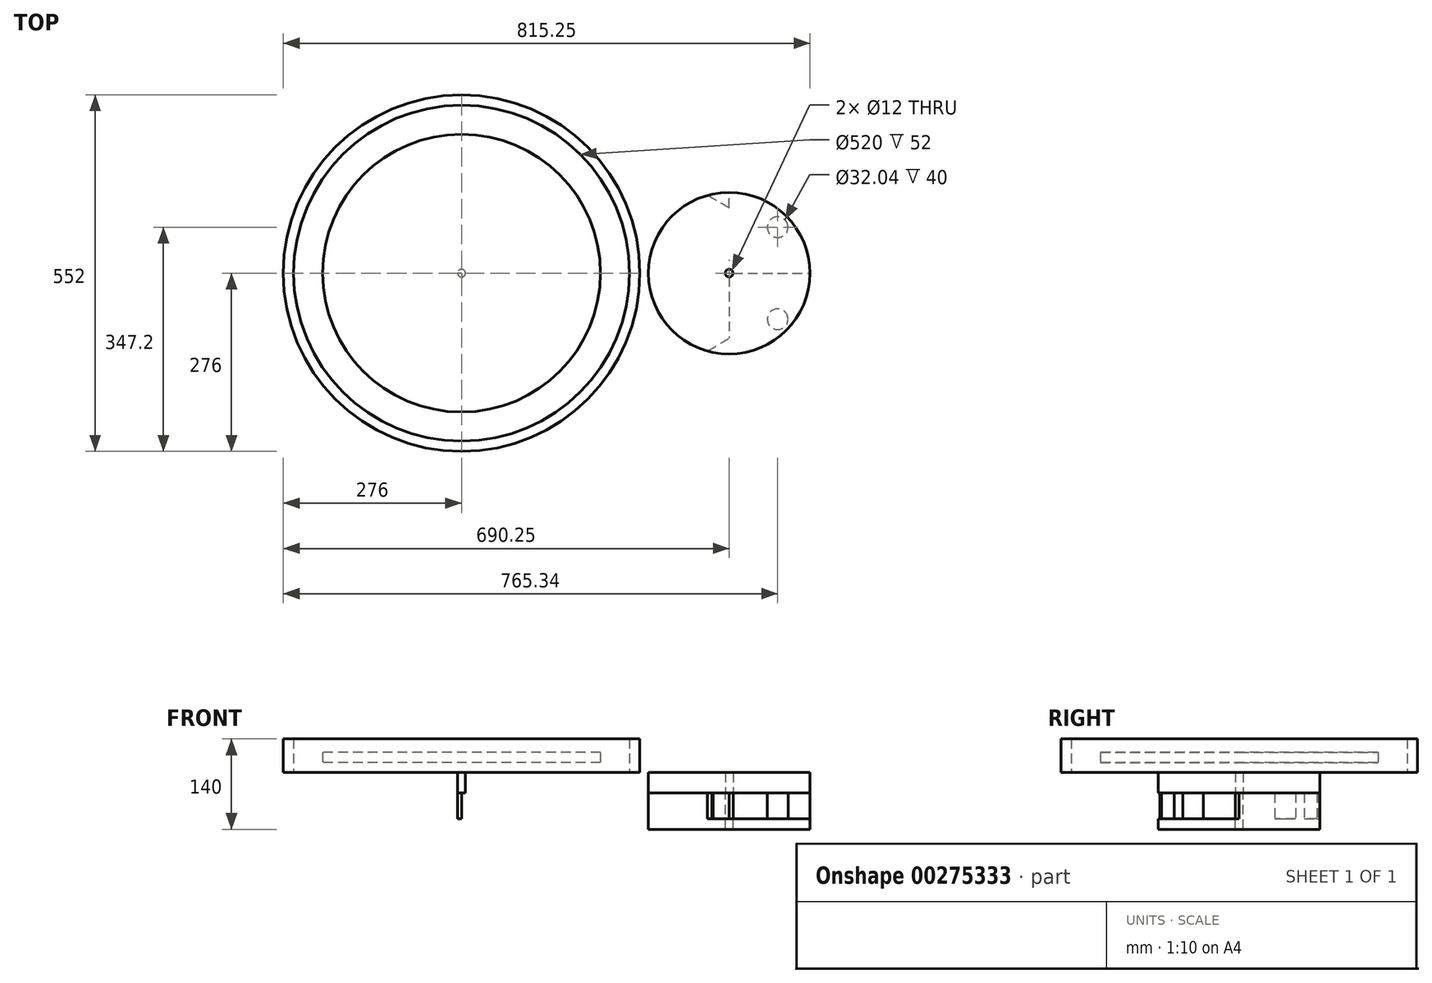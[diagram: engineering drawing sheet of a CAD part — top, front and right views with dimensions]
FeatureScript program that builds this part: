
annotation { "Feature Type Name" : "Feature", "Feature Type Description" : "" }
export const myFeature = defineFeature(function(context is Context, id is Id, definition is map)
    precondition{}
    {
        {
            var Q0;
            Q0=qCreatedBy(makeId("Top.planeOp"),FACE);
            var sketch = newSketch(context, id + "F0", { "sketchPlane" : qUnion([Q0])});
            skCircle(sketch, "E0", {"center": v(0, 0) * mm, "radius": 215 * mm});
            skCircle(sketch, "E1", {"center": v(0, 0) * mm, "radius": 260 * mm});
            skCircle(sketch, "E2", {"center": v(0, 0) * mm, "radius": 276 * mm});
            skSolve(sketch);
        }
        {
            var Q0;
            Q0=makeQuery(id+"F0.imprint","IMPRINT",FACE,{"disambiguationData":[TD([[makeQuery(id+"F0.imprint","IMPRINT",EDGE,{"derivedFrom":sQuery(id+"F0.wireOp",EDGE,"E0")}),1.0]])]});
            extrude(context, id + "F1", {"entities" : qUnion([Q0]), "depth" : 15 * mm});
        }
        {
            var Q0;
            Q0=makeQuery(id+"F1.opExtrude","CAP_FACE",FACE,{"disambiguationData":[OSD([sQuery(id+"F0.wireOp",EDGE,"E0")])],"isStart":false});
            extrude(context, id + "F2", {"entities" : qUnion([Q0]), "depth" : 16 * mm});
        }
        {
            var Q0;
            Q0=makeQuery(id+"F1.opExtrude","CAP_FACE",FACE,{"disambiguationData":[OSD([sQuery(id+"F0.wireOp",EDGE,"E0")])],"isStart":true});
            extrude(context, id + "F3", {"entities" : qUnion([Q0]), "operationType" : NewBodyOperationType.REMOVE, "oppositeDirection" : true, "depth" : 15 * mm});
        }
        {
            var Q0;
            Q0=makeQuery(id+"F0.imprint","IMPRINT",FACE,{"disambiguationData":[TD([[makeQuery(id+"F0.imprint","IMPRINT",EDGE,{"derivedFrom":sQuery(id+"F0.wireOp",EDGE,"E1")}),-1.0]])]});
            extrude(context, id + "F4", {"entities" : qUnion([Q0]), "depth" : 52 * mm});
        }
        {
            var Q0;
            Q0=qCreatedBy(makeId("Front.planeOp"),FACE);
            var sketch = newSketch(context, id + "F5", { "sketchPlane" : qUnion([Q0])});
            skLineSegment(sketch, "E3.bottom", {"start": v(0, 0) * mm, "end": v(-275.72, 0) * mm});
            skLineSegment(sketch, "E3.left", {"start": v(0, 0) * mm, "end": v(0, -16) * mm});
            skLineSegment(sketch, "E3.right", {"start": v(-275.72, 0) * mm, "end": v(-275.72, -16) * mm});
            skLineSegment(sketch, "E4.top", {"start": v(-275.72, -32) * mm, "end": v(0, -32) * mm});
            skLineSegment(sketch, "E4.left", {"start": v(-275.72, -16) * mm, "end": v(-275.72, -32) * mm});
            skLineSegment(sketch, "E4.right", {"start": v(0, -16) * mm, "end": v(0, -32) * mm});
            skFitSpline(sketch, "E5", {"points": [v(-259.93, 0) * mm, v(-213.05, -20.4) * mm, v(-60.25, 0) * mm], "startDerivative": vector(75.22, -131.35) * mm, "endDerivative": vector(230.25, 0) * mm});
            skLineSegment(sketch, "E6", {"start": v(-275.72, 0) * mm, "end": v(-259.93, 0) * mm});
            skLineSegment(sketch, "E7", {"start": v(0, 0) * mm, "end": v(-60.25, 0) * mm});
            skLineSegment(sketch, "E8", {"start": v(-275.72, 0) * mm, "end": v(-275.72, -32) * mm});
            skLineSegment(sketch, "E9.bottom", {"start": v(0, -32) * mm, "end": v(-6, -32) * mm});
            skLineSegment(sketch, "E9.top", {"start": v(0, 0) * mm, "end": v(-6, 0) * mm});
            skLineSegment(sketch, "E9.left", {"start": v(0, -32) * mm, "end": v(0, 0) * mm});
            skLineSegment(sketch, "E9.right", {"start": v(-6, -32) * mm, "end": v(-6, 0) * mm});
            skSolve(sketch);
        }
        {
            var Q0;
            Q0=makeQuery(id+"F5.imprint","IMPRINT",FACE,{"disambiguationData":[TD([[makeQuery(id+"F5.imprint","IMPRINT",EDGE,{"derivedFrom":sQuery(id+"F5.wireOp",EDGE,"E4.top")}),1.0]])]});
            var Q1;
            Q1=sQuery(id+"F5.wireOp",EDGE,"E4.right");
            revolve(context, id + "F6", {"entities" : qUnion([Q0]), "axis" : qUnion([Q1]), "revolveType" : RevolveType.FULL});
        }
        {
            var Q0;
            Q0=makeQuery(id+"F6.opRevolve","SWEPT_FACE",FACE,{"disambiguationData":[OSD([sQuery(id+"F5.wireOp",EDGE,"E4.top")])]});
            var sketch = newSketch(context, id + "F7", { "sketchPlane" : qUnion([Q0])});
            skCircle(sketch, "E10", {"center": v(414.25, 0) * mm, "radius": 125 * mm});
            skFitSpline(sketch, "E11", {"points": [v(501.83, 89.19) * mm, v(274.86, 218) * mm, v(0, 275.72) * mm], "startDerivative": vector(-181.97, 266.91) * mm, "endDerivative": vector(-537.63, 15.29) * mm});
            skLineSegment(sketch, "E12", {"start": v(414.25, 0) * mm, "end": v(0, 0) * mm});
            skFitSpline(sketch, "E13.MirrorCS", {"points": [v(501.83, -89.19) * mm, v(274.86, -218) * mm, v(0, -275.72) * mm], "startDerivative": vector(-181.97, -266.91) * mm, "endDerivative": vector(-537.63, -15.29) * mm});
            skFitSpline(sketch, "E14.MirrorCS", {"points": [v(501.83, -89.19) * mm, v(274.86, -218) * mm, v(0, -275.72) * mm], "startDerivative": vector(-181.97, -266.91) * mm, "endDerivative": vector(-537.63, -15.29) * mm});
            skLineSegment(sketch, "E15", {"start": v(0, 261.43) * mm, "end": v(0, 275.72) * mm});
            skLineSegment(sketch, "E16", {"start": v(0, -262.66) * mm, "end": v(0, -275.72) * mm});
            skArc(sketch, "E17", {"start": v(0, -262.66) * mm, "mid": v(263.36, -0.62) * mm, "end": v(0, 261.43) * mm});
            skCircle(sketch, "E18", {"center": v(414.25, 0) * mm, "radius": 6 * mm});
            skSolve(sketch);
        }
        {
            var Q0;
            Q0 = qSketchRegion(id + "F7", true);
            extrude(context, id + "F8", {"entities" : qUnion([Q0]), "operationType" : NewBodyOperationType.ADD, "oppositeDirection" : true, "depth" : 32 * mm});
        }
        {
            var Q0;
            Q0=makeQuery(id+"F8.boolean.opBoolean","MERGE",FACE,{"derivedFrom":[makeQuery(id+"F6.opRevolve","SWEPT_FACE",FACE,{"disambiguationData":[OSD([sQuery(id+"F5.wireOp",EDGE,"E4.top")])]}),makeQuery(id+"F8.opExtrude","CAP_FACE",FACE,{"disambiguationData":[OSD([sQuery(id+"F7.wireOp",EDGE,"E10"),sQuery(id+"F7.wireOp",EDGE,"E11"),sQuery(id+"F7.wireOp",EDGE,"E14.MirrorCS"),sQuery(id+"F7.wireOp",EDGE,"E15"),sQuery(id+"F7.wireOp",EDGE,"E16"),sQuery(id+"F7.wireOp",EDGE,"E17"),sQuery(id+"F7.wireOp",EDGE,"E18")])],"isStart":true})]});
            extrude(context, id + "F9", {"entities" : qUnion([Q0]), "depth" : 40 * mm});
        }
        {
            var Q0;
            Q0=makeQuery(id+"F9.opExtrude","CAP_FACE",FACE,{"disambiguationData":[OSD([sQuery(id+"F5.wireOp",EDGE,"E4.top"),sQuery(id+"F7.wireOp",EDGE,"E10"),sQuery(id+"F7.wireOp",EDGE,"E11"),sQuery(id+"F7.wireOp",EDGE,"E14.MirrorCS"),sQuery(id+"F7.wireOp",EDGE,"E15"),sQuery(id+"F7.wireOp",EDGE,"E16"),sQuery(id+"F7.wireOp",EDGE,"E17"),sQuery(id+"F7.wireOp",EDGE,"E18")])],"isStart":false});
            extrude(context, id + "F10", {"entities" : qUnion([Q0]), "depth" : 16 * mm});
        }
        {
            var Q0;
            Q0=makeQuery(id+"F9.opExtrude","CAP_FACE",FACE,{"disambiguationData":[OSD([sQuery(id+"F5.wireOp",EDGE,"E4.top"),sQuery(id+"F7.wireOp",EDGE,"E10"),sQuery(id+"F7.wireOp",EDGE,"E11"),sQuery(id+"F7.wireOp",EDGE,"E14.MirrorCS"),sQuery(id+"F7.wireOp",EDGE,"E15"),sQuery(id+"F7.wireOp",EDGE,"E16"),sQuery(id+"F7.wireOp",EDGE,"E17"),sQuery(id+"F7.wireOp",EDGE,"E18")])],"isStart":false});
            var sketch = newSketch(context, id + "F11", { "sketchPlane" : qUnion([Q0])});
            skCircle(sketch, "E19", {"center": v(0, 0) * mm, "radius": 249 * mm});
            skLineSegment(sketch, "E20", {"start": v(0, 0) * mm, "end": v(-303.54, 0) * mm});
            skPoint(sketch, "E20.endSnap0", {"position": v(-275.72, 0) * mm});
            skLineSegment(sketch, "E21", {"start": v(0, 0) * mm, "end": v(543.1, 0) * mm});
            skPoint(sketch, "E21.endSnap0", {"position": v(539.25, 0) * mm});
            skLineSegment(sketch, "E22", {"start": v(0, 0) * mm, "end": v(0, 284.87) * mm});
            skLineSegment(sketch, "E23", {"start": v(414.25, 0) * mm, "end": v(414.25, 300.96) * mm});
            skLineSegment(sketch, "E24.MirrorCS", {"start": v(414.25, 0) * mm, "end": v(414.25, -300.96) * mm});
            skLineSegment(sketch, "E25.MirrorCS", {"start": v(0, 0) * mm, "end": v(0, -284.87) * mm});
            skArc(sketch, "E26", {"start": v(-260.03, 91.7) * mm, "mid": v(-252.24, 72.81) * mm, "end": v(-234.67, 83.25) * mm});
            skArc(sketch, "E27", {"start": v(-30.78, 247.1) * mm, "mid": v(-22.5, 263.6) * mm, "end": v(-38.37, 273.04) * mm});
            skArc(sketch, "E28.MirrorCS", {"start": v(-30.78, -247.1) * mm, "mid": v(-22.5, -263.6) * mm, "end": v(-38.37, -273.04) * mm});
            skArc(sketch, "E29.MirrorCS", {"start": v(-260.03, -91.7) * mm, "mid": v(-252.24, -72.81) * mm, "end": v(-234.67, -83.25) * mm});
            skArc(sketch, "E30", {"start": v(462.1, 69.9) * mm, "mid": v(241.34, 186) * mm, "end": v(0, 249) * mm});
            skArc(sketch, "E31", {"start": v(373.84, 124.15) * mm, "mid": v(405.14, 135.2) * mm, "end": v(394.09, 166.5) * mm});
            skArc(sketch, "E32", {"start": v(191.52, 245.4) * mm, "mid": v(166.7, 232.73) * mm, "end": v(179.37, 207.9) * mm});
            skArc(sketch, "E33.MirrorCS", {"start": v(191.52, -245.4) * mm, "mid": v(166.7, -232.73) * mm, "end": v(179.37, -207.9) * mm});
            skArc(sketch, "E34.MirrorCS", {"start": v(462.1, -69.9) * mm, "mid": v(241.34, -186) * mm, "end": v(0, -249) * mm});
            skArc(sketch, "E35.MirrorCS", {"start": v(373.84, -124.15) * mm, "mid": v(405.14, -135.2) * mm, "end": v(394.09, -166.5) * mm});
            skCircle(sketch, "E36", {"center": v(489.34, 71.2) * mm, "radius": 16.02 * mm});
            skCircle(sketch, "E37.MirrorC", {"center": v(489.34, -71.2) * mm, "radius": 16.02 * mm});
            skSolve(sketch);
        }
        {
            var Q0;
            {var subQ1=sQuery(id+"F11.wireOp",EDGE,"E33.MirrorCS");Q0=makeQuery(id+"F11.imprint","IMPRINT",FACE,{"disambiguationData":[TD([[makeQuery(id+"F11.imprint","IMPRINT",EDGE,{"derivedFrom":subQ1}),1.0]])]});}
            var Q1;
            {var subQ6=sQuery(id+"F11.wireOp",EDGE,"E19");var subQ8=sQuery(id+"F11.wireOp",EDGE,"E21");var subQ10=makeQuery(id+"F11.imprint","INTERSECT",VERTEX,{"derivedFrom":[subQ6,subQ8]});Q1=makeQuery(id+"F11.imprint","IMPRINT",FACE,{"disambiguationData":[TD([[makeQuery(id+"F11.imprint","IMPRINT",EDGE,{"disambiguationData":[TD([[subQ10,1.0]])],"derivedFrom":subQ6}),-1.0]])]});}
            var Q2;
            {var subQ2=sQuery(id+"F11.wireOp",EDGE,"E19");var subQ7=sQuery(id+"F11.wireOp",EDGE,"E21");var subQ8=makeQuery(id+"F11.imprint","INTERSECT",VERTEX,{"derivedFrom":[subQ2,subQ7]});Q2=makeQuery(id+"F11.imprint","IMPRINT",FACE,{"disambiguationData":[TD([[makeQuery(id+"F11.imprint","IMPRINT",EDGE,{"disambiguationData":[TD([[subQ8,1.0]])],"derivedFrom":subQ2}),1.0]])]});}
            var Q3;
            Q3=makeQuery(id+"F11.imprint","IMPRINT",FACE,{"disambiguationData":[TD([[makeQuery(id+"F11.imprint","IMPRINT",EDGE,{"derivedFrom":sQuery(id+"F11.wireOp",EDGE,"E37.MirrorC")}),1.0]])]});
            var Q4;
            {var subQ0=sQuery(id+"F11.wireOp",EDGE,"E34.MirrorCS");var subQ1=sQuery(id+"F11.wireOp",EDGE,"E24.MirrorCS");var subQ2=makeQuery(id+"F11.imprint","INTERSECT",VERTEX,{"derivedFrom":[subQ1,subQ0]});Q4=makeQuery(id+"F11.imprint","IMPRINT",FACE,{"disambiguationData":[TD([[makeQuery(id+"F11.imprint","IMPRINT",EDGE,{"disambiguationData":[TD([[subQ2,-1.0]])],"derivedFrom":subQ1}),-1.0]])]});}
            var Q5;
            {var subQ0=sQuery(id+"F11.wireOp",EDGE,"E20");var subQ1=sQuery(id+"F11.wireOp",EDGE,"E19");var subQ2=makeQuery(id+"F11.imprint","INTERSECT",VERTEX,{"derivedFrom":[subQ1,subQ0]});Q5=makeQuery(id+"F11.imprint","IMPRINT",FACE,{"disambiguationData":[TD([[makeQuery(id+"F11.imprint","IMPRINT",EDGE,{"disambiguationData":[TD([[subQ2,-1.0]])],"derivedFrom":subQ1}),1.0]])]});}
            var Q6;
            {var subQ0=sQuery(id+"F11.wireOp",EDGE,"E28.MirrorCS");var subQ1=sQuery(id+"F11.wireOp",EDGE,"E19");var subQ2=makeQuery(id+"F11.imprint","INTERSECT",VERTEX,{"derivedFrom":[subQ1,subQ0]});Q6=makeQuery(id+"F11.imprint","IMPRINT",FACE,{"disambiguationData":[TD([[makeQuery(id+"F11.imprint","IMPRINT",EDGE,{"disambiguationData":[TD([[subQ2,-1.0]])],"derivedFrom":subQ1}),-1.0]])]});}
            var Q7;
            {var subQ0=sQuery(id+"F11.wireOp",EDGE,"E20");var subQ1=sQuery(id+"F11.wireOp",EDGE,"E19");var subQ2=makeQuery(id+"F11.imprint","INTERSECT",VERTEX,{"derivedFrom":[subQ1,subQ0]});Q7=makeQuery(id+"F11.imprint","IMPRINT",FACE,{"disambiguationData":[TD([[makeQuery(id+"F11.imprint","IMPRINT",EDGE,{"disambiguationData":[TD([[subQ2,-1.0]])],"derivedFrom":subQ1}),-1.0]])]});}
            var Q8;
            {var subQ1=sQuery(id+"F11.wireOp",EDGE,"E19");var subQ5=sQuery(id+"F11.wireOp",EDGE,"E26");var subQ6=makeQuery(id+"F11.imprint","INTERSECT",VERTEX,{"disambiguationData":[OD(0.0)],"derivedFrom":[subQ1,subQ5]});Q8=makeQuery(id+"F11.imprint","IMPRINT",FACE,{"disambiguationData":[TD([[makeQuery(id+"F11.imprint","IMPRINT",EDGE,{"disambiguationData":[TD([[subQ6,1.0]])],"derivedFrom":subQ1}),1.0]])]});}
            var Q9;
            {var subQ0=sQuery(id+"F11.wireOp",EDGE,"E26");var subQ1=sQuery(id+"F11.wireOp",EDGE,"E19");var subQ2=makeQuery(id+"F11.imprint","INTERSECT",VERTEX,{"disambiguationData":[OD(1.0)],"derivedFrom":[subQ1,subQ0]});Q9=makeQuery(id+"F11.imprint","IMPRINT",FACE,{"disambiguationData":[TD([[makeQuery(id+"F11.imprint","IMPRINT",EDGE,{"disambiguationData":[TD([[subQ2,-1.0]])],"derivedFrom":subQ1}),-1.0]])]});}
            var Q10;
            {var subQ0=sQuery(id+"F11.wireOp",EDGE,"E27");var subQ1=sQuery(id+"F11.wireOp",EDGE,"E19");var subQ2=makeQuery(id+"F11.imprint","INTERSECT",VERTEX,{"derivedFrom":[subQ1,subQ0]});Q10=makeQuery(id+"F11.imprint","IMPRINT",FACE,{"disambiguationData":[TD([[makeQuery(id+"F11.imprint","IMPRINT",EDGE,{"disambiguationData":[TD([[subQ2,1.0]])],"derivedFrom":subQ1}),-1.0]])]});}
            var Q11;
            {var subQ0=sQuery(id+"F11.wireOp",EDGE,"E32");Q11=makeQuery(id+"F11.imprint","IMPRINT",FACE,{"disambiguationData":[TD([[makeQuery(id+"F11.imprint","IMPRINT",EDGE,{"derivedFrom":subQ0}),-1.0]])]});}
            var Q12;
            {var subQ0=sQuery(id+"F11.wireOp",EDGE,"E30");var subQ2=sQuery(id+"F11.wireOp",EDGE,"E19");var subQ6=makeQuery(id+"F11.imprint","INTERSECT",VERTEX,{"derivedFrom":[subQ2,subQ0]});Q12=makeQuery(id+"F11.imprint","IMPRINT",FACE,{"disambiguationData":[TD([[makeQuery(id+"F11.imprint","IMPRINT",EDGE,{"disambiguationData":[TD([[subQ6,1.0]])],"derivedFrom":subQ2}),1.0]])]});}
            var Q13;
            {var subQ0=sQuery(id+"F11.wireOp",EDGE,"E30");var subQ7=sQuery(id+"F11.wireOp",EDGE,"E19");var subQ10=makeQuery(id+"F11.imprint","INTERSECT",VERTEX,{"derivedFrom":[subQ7,subQ0]});Q13=makeQuery(id+"F11.imprint","IMPRINT",FACE,{"disambiguationData":[TD([[makeQuery(id+"F11.imprint","IMPRINT",EDGE,{"disambiguationData":[TD([[subQ10,1.0]])],"derivedFrom":subQ7}),-1.0]])]});}
            var Q14;
            Q14=makeQuery(id+"F11.imprint","IMPRINT",FACE,{"disambiguationData":[TD([[makeQuery(id+"F11.imprint","IMPRINT",EDGE,{"derivedFrom":sQuery(id+"F11.wireOp",EDGE,"E36")}),-1.0]])]});
            var Q15;
            {var subQ0=sQuery(id+"F11.wireOp",EDGE,"E30");var subQ1=sQuery(id+"F11.wireOp",EDGE,"E23");var subQ2=makeQuery(id+"F11.imprint","INTERSECT",VERTEX,{"derivedFrom":[subQ1,subQ0]});Q15=makeQuery(id+"F11.imprint","IMPRINT",FACE,{"disambiguationData":[TD([[makeQuery(id+"F11.imprint","IMPRINT",EDGE,{"disambiguationData":[TD([[subQ2,-1.0]])],"derivedFrom":subQ1}),1.0]])]});}
            var Q16;
            {var subQ0=sQuery(id+"F11.wireOp",EDGE,"E34.MirrorCS");var subQ1=sQuery(id+"F11.wireOp",EDGE,"E19");var subQ3=makeQuery(id+"F11.imprint","INTERSECT",VERTEX,{"derivedFrom":[subQ1,subQ0]});Q16=makeQuery(id+"F11.imprint","IMPRINT",FACE,{"disambiguationData":[TD([[makeQuery(id+"F11.imprint","IMPRINT",EDGE,{"disambiguationData":[TD([[subQ3,1.0]])],"derivedFrom":subQ1}),1.0]])]});}
            var Q17;
            {var subQ0=sQuery(id+"F11.wireOp",EDGE,"E30");var subQ1=sQuery(id+"F11.wireOp",EDGE,"E19");var subQ3=makeQuery(id+"F11.imprint","INTERSECT",VERTEX,{"derivedFrom":[subQ1,subQ0]});Q17=makeQuery(id+"F11.imprint","IMPRINT",FACE,{"disambiguationData":[TD([[makeQuery(id+"F11.imprint","IMPRINT",EDGE,{"disambiguationData":[TD([[subQ3,-1.0]])],"derivedFrom":subQ1}),1.0]])]});}
            extrude(context, id + "F12", {"entities" : qUnion([Q0, Q1, Q2, Q3, Q4, Q5, Q6, Q7, Q8, Q9, Q10, Q11, Q12, Q13, Q14, Q15, Q16, Q17]), "operationType" : NewBodyOperationType.REMOVE, "oppositeDirection" : true, "depth" : 40 * mm});
        }
        {
            var Q0;
            Q0=makeQuery(id+"F12.boolean.opBoolean","SPLIT",FACE,{"disambiguationData":[TD([makeQuery(id+"F12.opExtrude","SWEPT_FACE",FACE,{"disambiguationData":[OSD([sQuery(id+"F11.wireOp",EDGE,"E37.MirrorC")])]})])],"derivedFrom":makeQuery(id+"F9.opExtrude","CAP_FACE",FACE,{"disambiguationData":[OSD([sQuery(id+"F5.wireOp",EDGE,"E4.top"),sQuery(id+"F7.wireOp",EDGE,"E10"),sQuery(id+"F7.wireOp",EDGE,"E11"),sQuery(id+"F7.wireOp",EDGE,"E14.MirrorCS"),sQuery(id+"F7.wireOp",EDGE,"E15"),sQuery(id+"F7.wireOp",EDGE,"E16"),sQuery(id+"F7.wireOp",EDGE,"E17"),sQuery(id+"F7.wireOp",EDGE,"E18")])],"isStart":false})});
            var Q1;
            {var subQ0=sQuery(id+"F7.wireOp",EDGE,"E14.MirrorCS");Q1=makeQuery(id+"F12.boolean.opBoolean","SPLIT",FACE,{"disambiguationData":[TD([makeQuery(id+"F9.opExtrude","SWEPT_FACE",FACE,{"disambiguationData":[OSD([subQ0])]})])],"derivedFrom":makeQuery(id+"F9.opExtrude","CAP_FACE",FACE,{"disambiguationData":[OSD([sQuery(id+"F5.wireOp",EDGE,"E4.top"),sQuery(id+"F7.wireOp",EDGE,"E10"),sQuery(id+"F7.wireOp",EDGE,"E11"),subQ0,sQuery(id+"F7.wireOp",EDGE,"E15"),sQuery(id+"F7.wireOp",EDGE,"E16"),sQuery(id+"F7.wireOp",EDGE,"E17"),sQuery(id+"F7.wireOp",EDGE,"E18")])],"isStart":false})});}
            var Q2;
            {var subQ0=sQuery(id+"F5.wireOp",EDGE,"E4.top");var subQ1=sQuery(id+"F11.wireOp",EDGE,"E28.MirrorCS");Q2=makeQuery(id+"F12.boolean.opBoolean","SPLIT",FACE,{"disambiguationData":[TD([makeQuery(id+"F12.opExtrude","SWEPT_FACE",FACE,{"disambiguationData":[OSD([subQ1])]})])],"derivedFrom":makeQuery(id+"F9.opExtrude","CAP_FACE",FACE,{"disambiguationData":[OSD([subQ0,sQuery(id+"F7.wireOp",EDGE,"E10"),sQuery(id+"F7.wireOp",EDGE,"E11"),sQuery(id+"F7.wireOp",EDGE,"E14.MirrorCS"),sQuery(id+"F7.wireOp",EDGE,"E15"),sQuery(id+"F7.wireOp",EDGE,"E16"),sQuery(id+"F7.wireOp",EDGE,"E17"),sQuery(id+"F7.wireOp",EDGE,"E18")])],"isStart":false})});}
            var Q3;
            {var subQ0=sQuery(id+"F5.wireOp",EDGE,"E4.top");var subQ1=sQuery(id+"F11.wireOp",EDGE,"E26");Q3=makeQuery(id+"F12.boolean.opBoolean","SPLIT",FACE,{"disambiguationData":[TD([makeQuery(id+"F12.opExtrude","SWEPT_FACE",FACE,{"disambiguationData":[OSD([subQ1])]})])],"derivedFrom":makeQuery(id+"F9.opExtrude","CAP_FACE",FACE,{"disambiguationData":[OSD([subQ0,sQuery(id+"F7.wireOp",EDGE,"E10"),sQuery(id+"F7.wireOp",EDGE,"E11"),sQuery(id+"F7.wireOp",EDGE,"E14.MirrorCS"),sQuery(id+"F7.wireOp",EDGE,"E15"),sQuery(id+"F7.wireOp",EDGE,"E16"),sQuery(id+"F7.wireOp",EDGE,"E17"),sQuery(id+"F7.wireOp",EDGE,"E18")])],"isStart":false})});}
            var Q4;
            {var subQ0=sQuery(id+"F7.wireOp",EDGE,"E11");Q4=makeQuery(id+"F12.boolean.opBoolean","SPLIT",FACE,{"disambiguationData":[TD([makeQuery(id+"F9.opExtrude","SWEPT_FACE",FACE,{"disambiguationData":[OSD([subQ0])]})])],"derivedFrom":makeQuery(id+"F9.opExtrude","CAP_FACE",FACE,{"disambiguationData":[OSD([sQuery(id+"F5.wireOp",EDGE,"E4.top"),sQuery(id+"F7.wireOp",EDGE,"E10"),subQ0,sQuery(id+"F7.wireOp",EDGE,"E14.MirrorCS"),sQuery(id+"F7.wireOp",EDGE,"E15"),sQuery(id+"F7.wireOp",EDGE,"E16"),sQuery(id+"F7.wireOp",EDGE,"E17"),sQuery(id+"F7.wireOp",EDGE,"E18")])],"isStart":false})});}
            var Q5;
            Q5=makeQuery(id+"F12.boolean.opBoolean","SPLIT",FACE,{"disambiguationData":[TD([makeQuery(id+"F12.opExtrude","SWEPT_FACE",FACE,{"disambiguationData":[OSD([sQuery(id+"F11.wireOp",EDGE,"E36")])]})])],"derivedFrom":makeQuery(id+"F9.opExtrude","CAP_FACE",FACE,{"disambiguationData":[OSD([sQuery(id+"F5.wireOp",EDGE,"E4.top"),sQuery(id+"F7.wireOp",EDGE,"E10"),sQuery(id+"F7.wireOp",EDGE,"E11"),sQuery(id+"F7.wireOp",EDGE,"E14.MirrorCS"),sQuery(id+"F7.wireOp",EDGE,"E15"),sQuery(id+"F7.wireOp",EDGE,"E16"),sQuery(id+"F7.wireOp",EDGE,"E17"),sQuery(id+"F7.wireOp",EDGE,"E18")])],"isStart":false})});
            extrude(context, id + "F13", {"entities" : qUnion([Q0, Q1, Q2, Q3, Q4, Q5]), "operationType" : NewBodyOperationType.ADD, "depth" : 3 * mm});
        }
        {
            var Q0;
            Q0=makeQuery(id+"F12.boolean.opBoolean","SPLIT",BODY,{"disambiguationData":[OD(5.0)],"derivedFrom":makeQuery(id+"F9.opExtrude","SWEPT_BODY",BODY,{"disambiguationData":[OSD([sQuery(id+"F5.wireOp",EDGE,"E4.top"),sQuery(id+"F7.wireOp",EDGE,"E10"),sQuery(id+"F7.wireOp",EDGE,"E11"),sQuery(id+"F7.wireOp",EDGE,"E14.MirrorCS"),sQuery(id+"F7.wireOp",EDGE,"E15"),sQuery(id+"F7.wireOp",EDGE,"E16"),sQuery(id+"F7.wireOp",EDGE,"E17"),sQuery(id+"F7.wireOp",EDGE,"E18")])]})});
            var Q1;
            Q1=makeQuery(id+"F12.boolean.opBoolean","SPLIT",BODY,{"disambiguationData":[OD(1.0)],"derivedFrom":makeQuery(id+"F9.opExtrude","SWEPT_BODY",BODY,{"disambiguationData":[OSD([sQuery(id+"F5.wireOp",EDGE,"E4.top"),sQuery(id+"F7.wireOp",EDGE,"E10"),sQuery(id+"F7.wireOp",EDGE,"E11"),sQuery(id+"F7.wireOp",EDGE,"E14.MirrorCS"),sQuery(id+"F7.wireOp",EDGE,"E15"),sQuery(id+"F7.wireOp",EDGE,"E16"),sQuery(id+"F7.wireOp",EDGE,"E17"),sQuery(id+"F7.wireOp",EDGE,"E18")])]})});
            var Q2;
            Q2=makeQuery(id+"F12.boolean.opBoolean","SPLIT",BODY,{"disambiguationData":[OD(3.0)],"derivedFrom":makeQuery(id+"F9.opExtrude","SWEPT_BODY",BODY,{"disambiguationData":[OSD([sQuery(id+"F5.wireOp",EDGE,"E4.top"),sQuery(id+"F7.wireOp",EDGE,"E10"),sQuery(id+"F7.wireOp",EDGE,"E11"),sQuery(id+"F7.wireOp",EDGE,"E14.MirrorCS"),sQuery(id+"F7.wireOp",EDGE,"E15"),sQuery(id+"F7.wireOp",EDGE,"E16"),sQuery(id+"F7.wireOp",EDGE,"E17"),sQuery(id+"F7.wireOp",EDGE,"E18")])]})});
            var Q3;
            Q3=makeQuery(id+"F12.boolean.opBoolean","SPLIT",BODY,{"disambiguationData":[OD(2.0)],"derivedFrom":makeQuery(id+"F9.opExtrude","SWEPT_BODY",BODY,{"disambiguationData":[OSD([sQuery(id+"F5.wireOp",EDGE,"E4.top"),sQuery(id+"F7.wireOp",EDGE,"E10"),sQuery(id+"F7.wireOp",EDGE,"E11"),sQuery(id+"F7.wireOp",EDGE,"E14.MirrorCS"),sQuery(id+"F7.wireOp",EDGE,"E15"),sQuery(id+"F7.wireOp",EDGE,"E16"),sQuery(id+"F7.wireOp",EDGE,"E17"),sQuery(id+"F7.wireOp",EDGE,"E18")])]})});
            var Q4;
            Q4=makeQuery(id+"F12.boolean.opBoolean","SPLIT",BODY,{"disambiguationData":[OD(0.0)],"derivedFrom":makeQuery(id+"F9.opExtrude","SWEPT_BODY",BODY,{"disambiguationData":[OSD([sQuery(id+"F5.wireOp",EDGE,"E4.top"),sQuery(id+"F7.wireOp",EDGE,"E10"),sQuery(id+"F7.wireOp",EDGE,"E11"),sQuery(id+"F7.wireOp",EDGE,"E14.MirrorCS"),sQuery(id+"F7.wireOp",EDGE,"E15"),sQuery(id+"F7.wireOp",EDGE,"E16"),sQuery(id+"F7.wireOp",EDGE,"E17"),sQuery(id+"F7.wireOp",EDGE,"E18")])]})});
            var Q5;
            Q5=makeQuery(id+"F12.boolean.opBoolean","SPLIT",BODY,{"disambiguationData":[OD(4.0)],"derivedFrom":makeQuery(id+"F9.opExtrude","SWEPT_BODY",BODY,{"disambiguationData":[OSD([sQuery(id+"F5.wireOp",EDGE,"E4.top"),sQuery(id+"F7.wireOp",EDGE,"E10"),sQuery(id+"F7.wireOp",EDGE,"E11"),sQuery(id+"F7.wireOp",EDGE,"E14.MirrorCS"),sQuery(id+"F7.wireOp",EDGE,"E15"),sQuery(id+"F7.wireOp",EDGE,"E16"),sQuery(id+"F7.wireOp",EDGE,"E17"),sQuery(id+"F7.wireOp",EDGE,"E18")])]})});
            var Q6;
            Q6=makeQuery(id+"F10.opExtrude","SWEPT_BODY",BODY,{"disambiguationData":[OSD([sQuery(id+"F5.wireOp",EDGE,"E4.top"),sQuery(id+"F7.wireOp",EDGE,"E10"),sQuery(id+"F7.wireOp",EDGE,"E11"),sQuery(id+"F7.wireOp",EDGE,"E14.MirrorCS"),sQuery(id+"F7.wireOp",EDGE,"E15"),sQuery(id+"F7.wireOp",EDGE,"E16"),sQuery(id+"F7.wireOp",EDGE,"E17"),sQuery(id+"F7.wireOp",EDGE,"E18")])]});
            booleanBodies(context, id + "F14", {"operationType" : BooleanOperationType.SUBTRACTION, "tools" : qUnion([Q0, Q1, Q2, Q3, Q4, Q5]), "targets" : qUnion([Q6]), "keepTools" : true});
        }
    });
